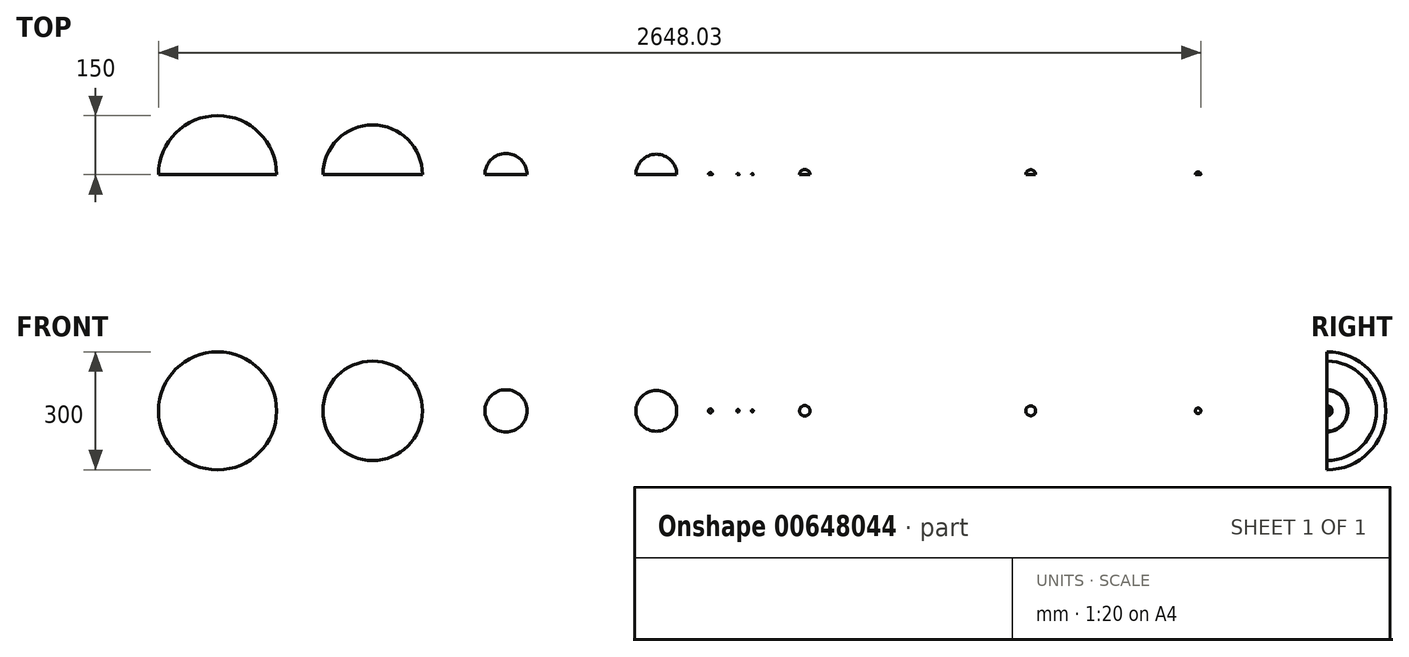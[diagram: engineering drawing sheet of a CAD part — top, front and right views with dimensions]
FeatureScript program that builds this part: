
annotation { "Feature Type Name" : "Feature", "Feature Type Description" : "" }
export const myFeature = defineFeature(function(context is Context, id is Id, definition is map)
    precondition{}
    {
        {
            var Q0;
            Q0=qCreatedBy(makeId("Front.planeOp"),FACE);
            var sketch = newSketch(context, id + "F0", { "sketchPlane" : qUnion([Q0])});
            skArc(sketch, "E0", {"start": v(-1165.18, 0) * mm, "mid": v(-1315.18, 150) * mm, "end": v(-1465.18, 0) * mm});
            skArc(sketch, "E1", {"start": v(-794.77, 0) * mm, "mid": v(-921.23, 126.45) * mm, "end": v(-1047.68, 0) * mm});
            skArc(sketch, "E2", {"start": v(-528.9, 0) * mm, "mid": v(-582.52, 53.63) * mm, "end": v(-636.15, 0) * mm});
            skArc(sketch, "E3", {"start": v(-148.68, 0) * mm, "mid": v(-200.58, 51.9) * mm, "end": v(-252.48, 0) * mm});
            skArc(sketch, "E4", {"start": v(189.86, 0) * mm, "mid": v(176.56, 13.3) * mm, "end": v(163.26, 0) * mm});
            skArc(sketch, "E5", {"start": v(763.27, 0) * mm, "mid": v(750.67, 12.6) * mm, "end": v(738.07, 0) * mm});
            skArc(sketch, "E6", {"start": v(1182.85, 0) * mm, "mid": v(1175.85, 7) * mm, "end": v(1168.85, 0) * mm});
            skLineSegment(sketch, "E7", {"start": v(-1165.18, 0) * mm, "end": v(-1465.18, 0) * mm});
            skLineSegment(sketch, "E8", {"start": v(-1047.68, 0) * mm, "end": v(-794.77, 0) * mm});
            skLineSegment(sketch, "E9", {"start": v(-636.15, 0) * mm, "end": v(-528.9, 0) * mm});
            skLineSegment(sketch, "E10", {"start": v(-252.48, 0) * mm, "end": v(-148.68, 0) * mm});
            skLineSegment(sketch, "E11", {"start": v(163.26, 0) * mm, "end": v(189.86, 0) * mm});
            skLineSegment(sketch, "E12", {"start": v(738.07, 0) * mm, "end": v(763.27, 0) * mm});
            skLineSegment(sketch, "E13", {"start": v(1168.85, 0) * mm, "end": v(1182.85, 0) * mm});
            skArc(sketch, "E14", {"start": v(-58.12, 0) * mm, "mid": v(-63.12, 5) * mm, "end": v(-68.12, 0) * mm});
            skArc(sketch, "E15", {"start": v(9.86, 0) * mm, "mid": v(6.86, 3) * mm, "end": v(3.86, 0) * mm});
            skLineSegment(sketch, "E16", {"start": v(-68.12, 0) * mm, "end": v(-58.12, 0) * mm});
            skLineSegment(sketch, "E17", {"start": v(3.86, 0) * mm, "end": v(9.86, 0) * mm});
            skArc(sketch, "E18", {"start": v(45.8, 0) * mm, "mid": v(43.3, 2.5) * mm, "end": v(40.8, 0) * mm});
            skLineSegment(sketch, "E19", {"start": v(40.8, 0) * mm, "end": v(45.8, 0) * mm});
            skSolve(sketch);
        }
        {
            var Q0;
            Q0 = qSketchRegion(id + "F0", true);
            var Q1;
            Q1=sQuery(id+"F0.wireOp",EDGE,"E7");
            revolve(context, id + "F1", {"entities" : qUnion([Q0]), "axis" : qUnion([Q1]), "revolveType" : RevolveType.ONE_DIRECTION, "angle" : 180 * degree});
        }
    });
